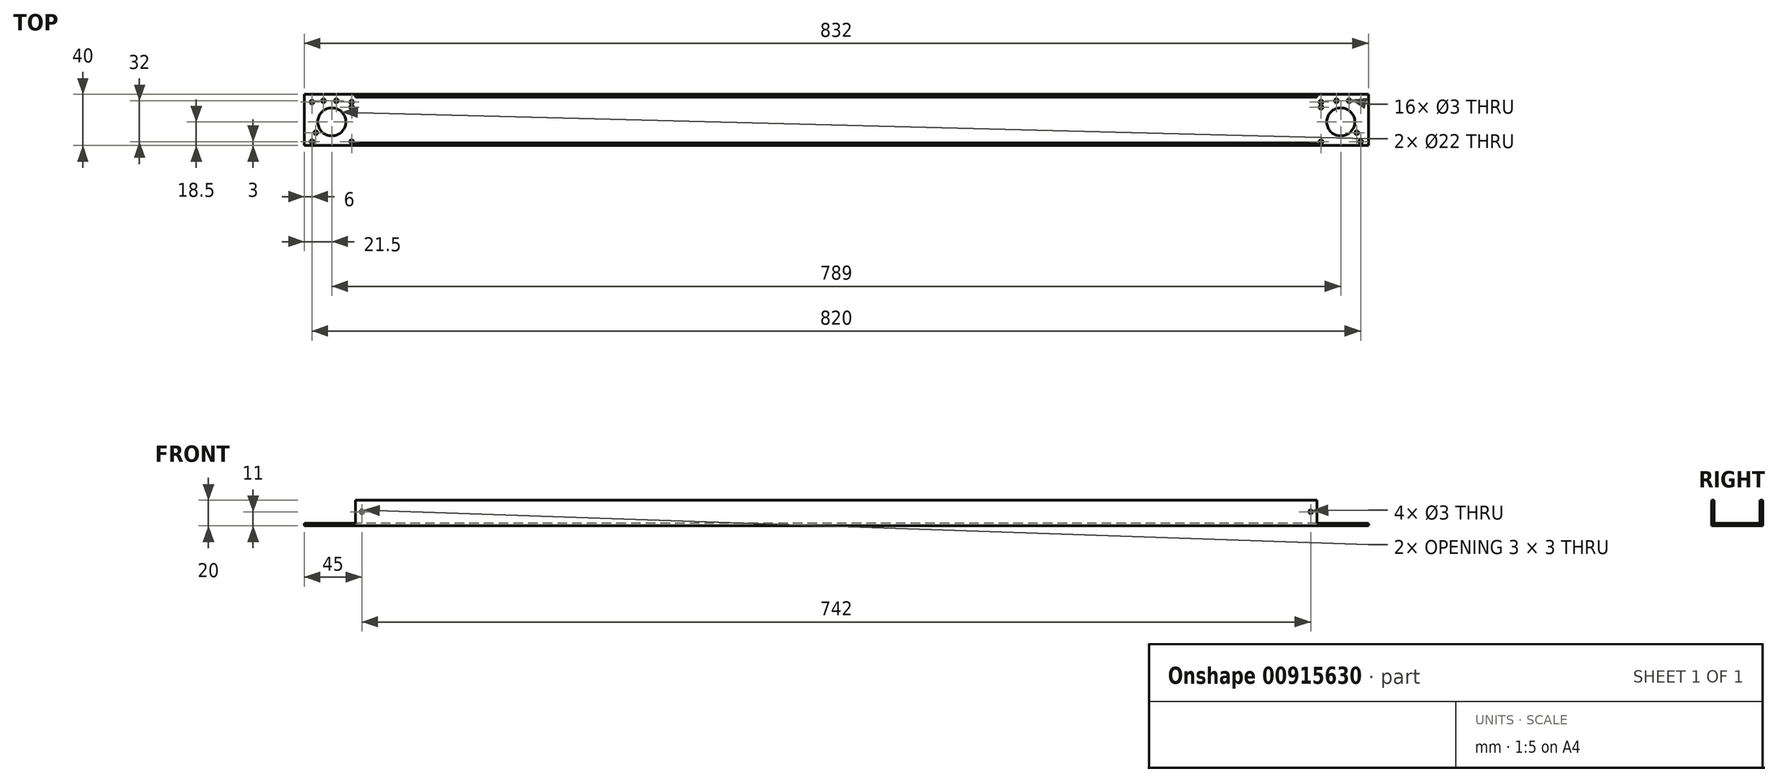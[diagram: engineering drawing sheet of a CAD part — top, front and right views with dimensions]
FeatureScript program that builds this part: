
annotation { "Feature Type Name" : "Feature", "Feature Type Description" : "" }
export const myFeature = defineFeature(function(context is Context, id is Id, definition is map)
    precondition{}
    {
        {
            var Q0;
            Q0=qCreatedBy(makeId("Right.planeOp"),FACE);
            var sketch = newSketch(context, id + "F0", { "sketchPlane" : qUnion([Q0])});
            skLineSegment(sketch, "E0.bottom", {"start": v(-20, 0) * mm, "end": v(20, 0) * mm});
            skLineSegment(sketch, "E0.top", {"start": v(-20, 20) * mm, "end": v(20, 20) * mm});
            skLineSegment(sketch, "E0.left", {"start": v(-20, 0) * mm, "end": v(-20, 20) * mm});
            skLineSegment(sketch, "E0.right", {"start": v(20, 0) * mm, "end": v(20, 20) * mm});
            skPoint(sketch, "E0.middle", {"position": v(0, 10) * mm});
            skLineSegment(sketch, "E1.bottom", {"start": v(-18, 20) * mm, "end": v(18, 20) * mm});
            skLineSegment(sketch, "E1.top", {"start": v(-18, 2) * mm, "end": v(18, 2) * mm});
            skLineSegment(sketch, "E1.left", {"start": v(-18, 20) * mm, "end": v(-18, 2) * mm});
            skLineSegment(sketch, "E1.right", {"start": v(18, 20) * mm, "end": v(18, 2) * mm});
            skPoint(sketch, "E1.middle", {"position": v(0, 11) * mm});
            skSolve(sketch);
        }
        {
            var Q0;
            Q0=makeQuery(id+"F0.imprint","IMPRINT",FACE,{"disambiguationData":[TD([[makeQuery(id+"F0.imprint","IMPRINT",EDGE,{"derivedFrom":sQuery(id+"F0.wireOp",EDGE,"E0.bottom")}),1.0]])]});
            extrude(context, id + "F1", {"entities" : qUnion([Q0]), "depth" : 416 * mm, "offsetDistance" : 25 * mm});
        }
        {
            var Q0;
            Q0=makeQuery(id+"F1.opExtrude","SWEPT_FACE",FACE,{"disambiguationData":[OSD([sQuery(id+"F0.wireOp",EDGE,"E0.right")])]});
            var sketch = newSketch(context, id + "F2", { "sketchPlane" : qUnion([Q0])});
            skLineSegment(sketch, "E2.bottom", {"start": v(-416, 20) * mm, "end": v(-376, 20) * mm});
            skLineSegment(sketch, "E2.top", {"start": v(-416, 2) * mm, "end": v(-376, 2) * mm});
            skLineSegment(sketch, "E2.left", {"start": v(-416, 20) * mm, "end": v(-416, 2) * mm});
            skLineSegment(sketch, "E2.right", {"start": v(-376, 20) * mm, "end": v(-376, 2) * mm});
            skSolve(sketch);
        }
        {
            var Q0;
            Q0=makeQuery(id+"F2.imprint","IMPRINT",FACE,{"disambiguationData":[TD([[makeQuery(id+"F2.imprint","IMPRINT",EDGE,{"derivedFrom":sQuery(id+"F2.wireOp",EDGE,"E2.bottom")}),-1.0]])]});
            var Q1;
            Q1 = qSketchRegion(id + "F4", true);
            extrude(context, id + "F3", {"entities" : qUnion([Q0, Q1]), "operationType" : NewBodyOperationType.REMOVE, "oppositeDirection" : true, "depth" : 100 * mm, "offsetDistance" : 25 * mm});
        }
        {
            var Q0;
            Q0=makeQuery(id+"F1.opExtrude","SWEPT_FACE",FACE,{"disambiguationData":[OSD([sQuery(id+"F0.wireOp",EDGE,"E0.bottom")])]});
            var sketch = newSketch(context, id + "F4", { "sketchPlane" : qUnion([Q0])});
            skLineSegment(sketch, "E3.bottom", {"start": v(410, 17) * mm, "end": v(379, 17) * mm});
            skLineSegment(sketch, "E3.top", {"start": v(410, -14) * mm, "end": v(379, -14) * mm});
            skLineSegment(sketch, "E3.left", {"start": v(410, 17) * mm, "end": v(410, -14) * mm});
            skLineSegment(sketch, "E3.right", {"start": v(379, 17) * mm, "end": v(379, -14) * mm});
            skPoint(sketch, "E4", {"position": v(394.5, 1.5) * mm});
            skPoint(sketch, "E4.positionSnap0", {"position": v(410, 1.5) * mm});
            skPoint(sketch, "E4.positionSnap1", {"position": v(394.5, 17) * mm});
            skCircle(sketch, "E5", {"center": v(394.5, 1.5) * mm, "radius": 11 * mm});
            skLineSegment(sketch, "E6.bottom", {"start": v(416, 20) * mm, "end": v(407, 20) * mm});
            skLineSegment(sketch, "E6.top", {"start": v(416, 10) * mm, "end": v(407, 10) * mm});
            skLineSegment(sketch, "E6.left", {"start": v(416, 20) * mm, "end": v(416, 10) * mm});
            skLineSegment(sketch, "E6.right", {"start": v(407, 20) * mm, "end": v(407, 10) * mm});
            skCircle(sketch, "E7", {"center": v(394.5, 1.5) * mm, "radius": 7 * mm, "construction": true});
            skCircle(sketch, "E8", {"center": v(407, 10) * mm, "radius": 6.5 * mm, "construction": true});
            skLineSegment(sketch, "E9.bottom", {"start": v(369, 17) * mm, "end": v(379, 17) * mm, "construction": true});
            skLineSegment(sketch, "E9.top", {"start": v(369, -10) * mm, "end": v(379, -10) * mm, "construction": true});
            skLineSegment(sketch, "E9.left", {"start": v(379, 17) * mm, "end": v(379, -10) * mm, "construction": true});
            skLineSegment(sketch, "E9.right", {"start": v(369, 17) * mm, "end": v(369, -10) * mm, "construction": true});
            skPoint(sketch, "E10", {"position": v(394.5, -14) * mm});
            skLineSegment(sketch, "E11.bottom", {"start": v(401, -18) * mm, "end": v(391, -18) * mm});
            skLineSegment(sketch, "E11.top", {"start": v(401, -15) * mm, "end": v(391, -15) * mm});
            skLineSegment(sketch, "E11.left", {"start": v(401, -18) * mm, "end": v(401, -15) * mm});
            skLineSegment(sketch, "E11.right", {"start": v(391, -18) * mm, "end": v(391, -15) * mm});
            skLineSegment(sketch, "E12.bottom", {"start": v(416, 20) * mm, "end": v(414, 20) * mm});
            skLineSegment(sketch, "E12.top", {"start": v(416, 18) * mm, "end": v(414, 18) * mm});
            skLineSegment(sketch, "E12.left", {"start": v(416, 20) * mm, "end": v(416, 18) * mm});
            skLineSegment(sketch, "E12.right", {"start": v(414, 20) * mm, "end": v(414, 18) * mm});
            skCircle(sketch, "E13", {"center": v(369, -10) * mm, "radius": 5 * mm, "construction": true});
            skCircle(sketch, "E14", {"center": v(407, 10) * mm, "radius": 5 * mm, "construction": true});
            skCircle(sketch, "E15", {"center": v(369, -10) * mm, "radius": 6.5 * mm, "construction": true});
            skSolve(sketch);
        }
        {
            var Q0;
            Q0=sQuery(id+"F4.wireOp",VERTEX,"E3.bottom.start");
            var Q1;
            Q1=sQuery(id+"F4.wireOp",VERTEX,"E3.top.start");
            var Q2;
            Q2=sQuery(id+"F4.wireOp",VERTEX,"E3.top.end");
            var Q3;
            Q3=sQuery(id+"F4.wireOp",VERTEX,"E3.bottom.end");
            var Q4;
            Q4=sQuery(id+"F4.wireOp",VERTEX,"MUwf6Tix-luRl-CnvR-nVcB-yN6IE4vDphWf.bottom.end");
            var Q5;
            Q5=sQuery(id+"F4.wireOp",VERTEX,"E6.top.end");
            var Q6;
            Q6=sQuery(id+"F4.wireOp",VERTEX,"E9.top.end");
            var Q7;
            Q7=sQuery(id+"F4.wireOp",VERTEX,"E11.top.end");
            var Q8;
            Q8=sQuery(id+"F4.wireOp",VERTEX,"E11.top.start");
            var Q9;
            Q9=sQuery(id+"F4.wireOp",VERTEX,"80c69b23-61b6-45ce-ae92-fe1352ea3409.positionSnap0");
            var Q10;
            Q10=makeQuery(id+"F1.opExtrude","SWEPT_BODY",BODY,{"disambiguationData":[OSD([sQuery(id+"F0.wireOp",EDGE,"E0.bottom"),sQuery(id+"F0.wireOp",EDGE,"E0.top"),sQuery(id+"F0.wireOp",EDGE,"E0.left"),sQuery(id+"F0.wireOp",EDGE,"E0.right"),sQuery(id+"F0.wireOp",EDGE,"E1.top"),sQuery(id+"F0.wireOp",EDGE,"E1.left"),sQuery(id+"F0.wireOp",EDGE,"E1.right")])]});
            hole(context, id + "F5", {"style" : HoleStyle.SIMPLE, "endStyle" : HoleEndStyle.BLIND, "holeDiameter" : 3 * mm, "majorDiameter" : 5 * mm, "holeDepth" : 50 * mm, "isTappedThrough" : true, "tappedDepth" : 12 * mm, "tapClearance" : 3, "locations" : qUnion([Q0, Q1, Q2, Q3, Q4, Q5, Q6, Q7, Q8, Q9]), "scope" : qUnion([Q10])});
        }
        {
            var Q0;
            Q0=makeQuery(id+"F4.imprint","IMPRINT",FACE,{"disambiguationData":[TD([[makeQuery(id+"F4.imprint","IMPRINT",EDGE,{"derivedFrom":sQuery(id+"F4.wireOp",EDGE,"E5")}),1.0]])]});
            extrude(context, id + "F6", {"entities" : qUnion([Q0]), "operationType" : NewBodyOperationType.REMOVE, "oppositeDirection" : true, "depth" : 25 * mm, "offsetDistance" : 25 * mm});
        }
        {
            var Q0;
            {var subQ0=makeQuery(id+"F1.opExtrude","SWEPT_FACE",FACE,{"disambiguationData":[OSD([sQuery(id+"F0.wireOp",EDGE,"E0.left")])]});Q0=makeQuery(id+"F9.boolean.opBoolean","MERGE",FACE,{"derivedFrom":[subQ0,makeQuery(id+"F9.opPattern","COPY",FACE,{"derivedFrom":subQ0,"instanceName":"1"})]});}
            var sketch = newSketch(context, id + "F7", { "sketchPlane" : qUnion([Q0])});
            skPoint(sketch, "E16.middle", {"position": v(376, 20) * mm});
            skLineSegment(sketch, "E17.bottom", {"start": v(376, 20) * mm, "end": v(371, 20) * mm});
            skLineSegment(sketch, "E17.top", {"start": v(376, 11) * mm, "end": v(371, 11) * mm});
            skLineSegment(sketch, "E17.left", {"start": v(376, 20) * mm, "end": v(376, 11) * mm});
            skLineSegment(sketch, "E17.right", {"start": v(371, 20) * mm, "end": v(371, 11) * mm});
            skSolve(sketch);
        }
        {
            var Q0;
            Q0=sQuery(id+"F7.wireOp",VERTEX,"E17.top.end");
            var Q1;
            Q1=makeQuery(id+"F1.opExtrude","SWEPT_BODY",BODY,{"disambiguationData":[OSD([sQuery(id+"F0.wireOp",EDGE,"E0.bottom"),sQuery(id+"F0.wireOp",EDGE,"E0.top"),sQuery(id+"F0.wireOp",EDGE,"E0.left"),sQuery(id+"F0.wireOp",EDGE,"E0.right"),sQuery(id+"F0.wireOp",EDGE,"E1.top"),sQuery(id+"F0.wireOp",EDGE,"E1.left"),sQuery(id+"F0.wireOp",EDGE,"E1.right")])]});
            hole(context, id + "F8", {"style" : HoleStyle.SIMPLE, "endStyle" : HoleEndStyle.THROUGH, "holeDiameter" : 3 * mm, "majorDiameter" : 5 * mm, "isTappedThrough" : true, "tappedDepth" : 12 * mm, "tapClearance" : 3, "locations" : qUnion([Q0]), "scope" : qUnion([Q1])});
        }
        {
            var Q0;
            Q0=makeQuery(id+"F1.opExtrude","SWEPT_BODY",BODY,{"disambiguationData":[OSD([sQuery(id+"F0.wireOp",EDGE,"E0.bottom"),sQuery(id+"F0.wireOp",EDGE,"E0.top"),sQuery(id+"F0.wireOp",EDGE,"E0.left"),sQuery(id+"F0.wireOp",EDGE,"E0.right"),sQuery(id+"F0.wireOp",EDGE,"E1.top"),sQuery(id+"F0.wireOp",EDGE,"E1.left"),sQuery(id+"F0.wireOp",EDGE,"E1.right")])]});
            var Q1;
            Q1=makeQuery(id+"F0.imprint","IMPRINT",FACE,{"disambiguationData":[TD([[makeQuery(id+"F0.imprint","IMPRINT",EDGE,{"derivedFrom":sQuery(id+"F0.wireOp",EDGE,"E0.bottom")}),1.0]])]});
            mirror(context, id + "F9", {"operationType" : NewBodyOperationType.ADD, "entities" : qUnion([Q0]), "mirrorPlane" : qUnion([Q1])});
        }
    });
